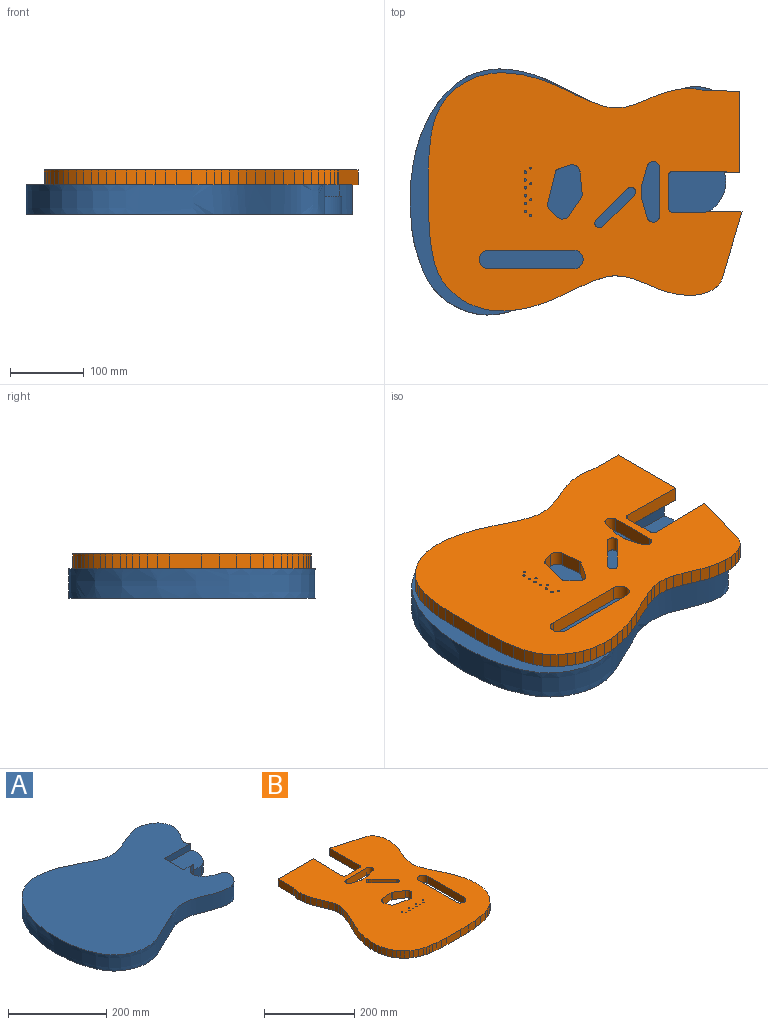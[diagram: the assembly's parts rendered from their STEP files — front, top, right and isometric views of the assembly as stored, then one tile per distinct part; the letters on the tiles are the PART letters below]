
ASSEMBLY  parts=2 mates=1
PART A: 11 faces, bbox 445.4x335.9x40 mm
  f0: plane 50x16mm, normal (1,0,0), area 800mm2, adj f1,f6,f9,f10
  f1: plane 445.41x335.86mm, normal (0,0,1), area 106671.7mm2, adj f0,f2,f4,f5,f7,f9,f10
  f2: extruded ~442.1x331.43mm, area 53327mm2, adj f1,f3,f5,f6,f7,f8
  f3: plane 445.41x335.86mm, normal (0,0,-1), area 110689mm2, adj f2,f7,f8
  f4: plane 25.33x16mm, normal (-0.01,1,0), area 405.4mm2, adj f1,f6,f7,f10
  f5: plane 72.36x16mm, normal (-0.01,-1,0), area 1157.8mm2, adj f1,f2,f6,f9
  f6: plane 78.66x55.93mm, normal (0,0,1), area 4002.8mm2, adj f0,f2,f4,f5,f8,f9,f10
  f7: plane 40x0.32mm, normal (0.99,-0.13,0), area 12.8mm2, adj f1,f2,f3,f4,f8
  f8: plane 24x22.41mm, normal (0.01,-1,0), area 538mm2, adj f2,f3,f6,f7
  f9: cylinder r=3mm len=16mm, axis (0,0,-1), area 74.9mm2, adj f0,f1,f5,f6
  f10: cylinder r=3mm len=16mm, axis (0,0,-1), area 74.9mm2, adj f0,f1,f4,f6
PART B: 125 faces, bbox 324x426.6x20 mm
  f0: plane 20x4.05mm, normal (0.34,0.94,0), area 86.3mm2, adj f98,f117,f118,f122
  f1: cylinder r=6.35mm len=20mm, axis (0,0,-1), area 189.6mm2, adj f114,f117,f118,f124
  f2: cylinder r=6.35mm len=20mm, axis (0,0,-1), area 34.9mm2, adj f3,f116,f117,f118
  f3: plane 25x20mm, normal (0.27,0.96,0), area 519.5mm2, adj f2,f4,f117,f118
  f4: cylinder r=8.71mm len=20mm, axis (0,0,-1), area 499.5mm2, adj f3,f5,f117,f118
  f5: plane 65.13x20mm, normal (0,-1,0), area 1302.5mm2, adj f4,f6,f117,f118
  f6: cylinder r=8.71mm len=20mm, axis (0,0,-1), area 499.5mm2, adj f5,f7,f117,f118
  f7: plane 25x20mm, normal (-0.27,0.96,0), area 519.5mm2, adj f6,f8,f117,f118
  f8: cylinder r=6.35mm len=20mm, axis (0,0,-1), area 34.9mm2, adj f7,f116,f117,f118
  f9: cylinder r=6.73mm len=20mm, axis (0,0,-1), area 134.8mm2, adj f10,f102,f117,f118
  f10: plane 42.31x20mm, normal (0.24,0.97,0), area 872.1mm2, adj f9,f11,f117,f118
  f11: cylinder r=6.73mm len=20mm, axis (0,0,-1), area 134.8mm2, adj f10,f12,f117,f118
  f12: plane 20x15.05mm, normal (0.95,0.32,0), area 317.5mm2, adj f11,f13,f117,f118
  f13: cylinder r=10.92mm len=20mm, axis (0,0,-1), area 393.9mm2, adj f12,f14,f117,f118
  f14: plane 29.83x20mm, normal (0.09,-1,0), area 599mm2, adj f13,f15,f117,f118
  f15: cylinder r=6.73mm len=20mm, axis (0,0,-1), area 90.9mm2, adj f14,f16,f117,f118
  f16: plane 24.94x20mm, normal (-0.55,-0.83,0), area 597.4mm2, adj f15,f17,f117,f118
  f17: cylinder r=10.92mm len=20mm, axis (0,0,-1), area 393.7mm2, adj f16,f102,f117,f118
  f18: cylinder r=12.7mm len=25.4mm, axis (0,0,-1), area 798mm2, adj f19,f103,f117,f118
  f19: plane 116.08x20mm, normal (-1,0,0), area 2321.6mm2, adj f18,f20,f117,f118
  f20: cylinder r=12.7mm len=25.4mm, axis (0,0,-1), area 798mm2, adj f19,f103,f117,f118
  f21: cylinder r=6.35mm len=20mm, axis (0,0,-1), area 194mm2, adj f114,f117,f118,f120
  f22: plane 20x8.11mm, normal (-0.97,0.23,0), area 166.6mm2, adj f23,f117,f118,f119
  f23: plane 20x9.22mm, normal (-0.99,0.1,0), area 185.3mm2, adj f22,f24,f117,f118
  f24: plane 20x10.36mm, normal (-1,-0.01,0), area 207.3mm2, adj f23,f25,f117,f118
  f25: plane 20x11.54mm, normal (-0.99,-0.12,0), area 232.7mm2, adj f24,f26,f117,f118
  f26: plane 20x12.72mm, normal (-0.97,-0.24,0), area 262.2mm2, adj f25,f27,f117,f118
  f27: plane 20x13.71mm, normal (-0.94,-0.34,0), area 291mm2, adj f26,f28,f117,f118
  f28: plane 20x14.18mm, normal (-0.92,-0.38,0), area 307.1mm2, adj f27,f29,f117,f118
  f29: plane 20x13.85mm, normal (-0.93,-0.37,0), area 298.3mm2, adj f28,f30,f117,f118
  f30: plane 20x12.77mm, normal (-0.96,-0.29,0), area 266.5mm2, adj f29,f31,f117,f118
  f31: plane 20x11.39mm, normal (-0.99,-0.13,0), area 229.7mm2, adj f30,f32,f117,f118
  f32: plane 20x10.19mm, normal (-1,0.06,0), area 204.1mm2, adj f31,f33,f117,f118
  f33: plane 20x9.45mm, normal (-0.98,0.21,0), area 193.3mm2, adj f32,f34,f117,f118
  f34: plane 20x18.07mm, normal (-0.94,0.33,0), area 382.4mm2, adj f33,f35,f117,f118
  f35: plane 20x17.87mm, normal (-0.91,0.41,0), area 392.6mm2, adj f34,f36,f117,f118
  f36: plane 20x18.39mm, normal (-0.9,0.44,0), area 409.3mm2, adj f35,f37,f117,f118
  f37: plane 20x19.13mm, normal (-0.92,0.4,0), area 417mm2, adj f36,f38,f117,f118
  f38: plane 20x18.13mm, normal (-0.94,0.33,0), area 384.7mm2, adj f37,f39,f117,f118
  f39: plane 20x16.67mm, normal (-0.97,0.25,0), area 343.9mm2, adj f38,f40,f117,f118
  f40: plane 20x17.8mm, normal (-0.99,0.14,0), area 359.3mm2, adj f39,f41,f117,f118
  f41: plane 20x12.37mm, normal (-1,0.05,0), area 247.7mm2, adj f40,f42,f117,f118
  f42: plane 20x11.55mm, normal (-1,-0.05,0), area 231.2mm2, adj f41,f43,f117,f118
  f43: plane 20x10.2mm, normal (-0.99,-0.16,0), area 206.7mm2, adj f42,f44,f117,f118
  f44: plane 20x13.46mm, normal (-0.96,-0.28,0), area 280.2mm2, adj f43,f45,f117,f118
  f45: plane 20x12.96mm, normal (-0.91,-0.41,0), area 284.4mm2, adj f44,f46,f117,f118
  f46: plane 20x6.84mm, normal (-0.85,-0.52,0), area 160.6mm2, adj f45,f47,f117,f118
  f47: plane 20x7.21mm, normal (-0.8,-0.6,0), area 180.2mm2, adj f46,f48,f117,f118
  f48: plane 20x7.52mm, normal (-0.74,-0.67,0), area 203.8mm2, adj f47,f49,f117,f118
  f49: plane 20x8.84mm, normal (-0.65,-0.76,0), area 233.7mm2, adj f48,f50,f117,f118
  f50: plane 20x7.47mm, normal (-0.56,-0.83,0), area 179.6mm2, adj f49,f51,f117,f118
  f51: plane 20x9.22mm, normal (-0.46,-0.89,0), area 207.3mm2, adj f50,f52,f117,f118
  f52: plane 20x11.57mm, normal (-0.35,-0.94,0), area 246.8mm2, adj f51,f53,f117,f118
  f53: plane 20x6.99mm, normal (-0.27,-0.96,0), area 144.9mm2, adj f52,f54,f117,f118
  f54: plane 20x8.09mm, normal (-0.21,-0.98,0), area 165.4mm2, adj f53,f55,f117,f118
  f55: plane 20x9.49mm, normal (-0.16,-0.99,0), area 192.2mm2, adj f54,f56,f117,f118
  f56: plane 20x11.26mm, normal (-0.11,-0.99,0), area 226.7mm2, adj f55,f57,f117,f118
  f57: plane 20x13.47mm, normal (-0.08,-1,0), area 270.2mm2, adj f56,f58,f117,f118
  f58: plane 20x16.18mm, normal (-0.04,-1,0), area 324mm2, adj f57,f59,f117,f118
  f59: plane 43.54x20mm, normal (0,-1,0), area 870.8mm2, adj f58,f60,f117,f118
  f60: plane 24.61x20mm, normal (0.03,-1,0), area 492.3mm2, adj f59,f61,f117,f118
  f61: plane 22.94x20mm, normal (0.06,-1,0), area 459.7mm2, adj f60,f62,f117,f118
  f62: plane 20.06x20mm, normal (0.13,-0.99,0), area 404.5mm2, adj f61,f63,f117,f118
  f63: plane 20x16.76mm, normal (0.22,-0.98,0), area 343.6mm2, adj f62,f64,f117,f118
  f64: plane 20x13.56mm, normal (0.34,-0.94,0), area 288.5mm2, adj f63,f65,f117,f118
  f65: plane 20x10.83mm, normal (0.48,-0.88,0), area 246.9mm2, adj f64,f66,f117,f118
  f66: plane 20x8.81mm, normal (0.61,-0.79,0), area 222.5mm2, adj f65,f67,f117,f118
  f67: plane 20x7.42mm, normal (0.71,-0.7,0), area 209.1mm2, adj f66,f68,f117,f118
  f68: plane 20x10.27mm, normal (0.79,-0.61,0), area 260.2mm2, adj f67,f69,f117,f118
  f69: plane 20x10.03mm, normal (0.86,-0.51,0), area 232.9mm2, adj f68,f70,f117,f118
  f70: plane 20x9.7mm, normal (0.92,-0.4,0), area 211.6mm2, adj f69,f71,f117,f118
  f71: plane 20x9.98mm, normal (0.95,-0.3,0), area 209.3mm2, adj f70,f72,f117,f118
  f72: plane 20x11.06mm, normal (0.98,-0.2,0), area 225.7mm2, adj f71,f73,f117,f118
  f73: plane 20x12.75mm, normal (1,-0.08,0), area 255.8mm2, adj f72,f74,f117,f118
  f74: plane 20x14.01mm, normal (1,0.04,0), area 280.4mm2, adj f73,f75,f117,f118
  f75: plane 20x13.73mm, normal (0.99,0.12,0), area 276.5mm2, adj f74,f76,f117,f118
  f76: plane 20x12.74mm, normal (0.98,0.2,0), area 260.1mm2, adj f75,f77,f117,f118
  f77: plane 20x12.84mm, normal (0.96,0.28,0), area 267.6mm2, adj f76,f78,f117,f118
  f78: plane 20x13.94mm, normal (0.94,0.34,0), area 296.7mm2, adj f77,f79,f117,f118
  f79: plane 20x14.55mm, normal (0.92,0.39,0), area 316mm2, adj f78,f80,f117,f118
  f80: plane 21.12x20mm, normal (0.9,0.43,0), area 468.9mm2, adj f79,f81,f117,f118
  f81: plane 20.35x20mm, normal (0.91,0.41,0), area 447.4mm2, adj f80,f82,f117,f118
  f82: plane 20x10.22mm, normal (0.94,0.35,0), area 218mm2, adj f81,f83,f117,f118
  f83: plane 20x10.44mm, normal (0.96,0.28,0), area 217.3mm2, adj f82,f84,f117,f118
  f84: plane 20x11.04mm, normal (0.99,0.15,0), area 223.5mm2, adj f83,f85,f117,f118
  f85: plane 20x12.29mm, normal (1,-0.04,0), area 246mm2, adj f84,f86,f117,f118
  f86: plane 20x11.09mm, normal (0.97,-0.23,0), area 227.8mm2, adj f85,f87,f117,f118
  f87: plane 20x12.16mm, normal (0.94,-0.34,0), area 258.4mm2, adj f86,f88,f117,f118
  f88: plane 20x12.83mm, normal (0.92,-0.38,0), area 278mm2, adj f87,f89,f117,f118
  f89: plane 20x12.85mm, normal (0.93,-0.38,0), area 277.2mm2, adj f88,f90,f117,f118
  f90: plane 20x12.32mm, normal (0.95,-0.32,0), area 260mm2, adj f89,f91,f117,f118
  f91: plane 20x14.15mm, normal (0.98,-0.22,0), area 289.9mm2, adj f90,f92,f117,f118
  f92: plane 20x12.57mm, normal (1,-0.09,0), area 252.5mm2, adj f91,f93,f117,f118
  f93: plane 20x11.04mm, normal (1,0.03,0), area 220.8mm2, adj f92,f94,f117,f118
  f94: plane 20x9.63mm, normal (0.99,0.16,0), area 195.2mm2, adj f93,f95,f117,f118
  f95: plane 20x8.39mm, normal (0.95,0.32,0), area 177.4mm2, adj f94,f96,f117,f118
  f96: plane 20x7.16mm, normal (0.87,0.5,0), area 165.3mm2, adj f95,f97,f117,f118
  f97: plane 20x5.67mm, normal (0.75,0.66,0), area 151mm2, adj f96,f98,f117,f118
  f98: plane 20x5.18mm, normal (0.59,0.81,0), area 128.4mm2, adj f0,f97,f117,f118
  f99: cylinder r=6.35mm len=20mm, axis (0,0,-1), area 399mm2, adj f100,f115,f117,f118
  f100: plane 42.66x42.66mm, normal (0.71,0.71,0), area 1206.5mm2, adj f99,f101,f117,f118
  f101: cylinder r=6.35mm len=20mm, axis (0,0,-1), area 399mm2, adj f100,f115,f117,f118
  f102: plane 20x11.55mm, normal (-0.69,0.73,0), area 317.5mm2, adj f9,f17,f117,f118
  f103: plane 116.08x20mm, normal (1,0,0), area 2321.6mm2, adj f18,f20,f117,f118
  f104: cylinder r=1.38mm len=20mm, axis (0,0,-1), area 174mm2, adj f117,f118
  f105: cylinder r=1.38mm len=20mm, axis (0,0,-1), area 174mm2, adj f117,f118
  f106: cylinder r=1.59mm len=20mm, axis (0,0,-1), area 199.5mm2, adj f117,f118
  f107: cylinder r=1.59mm len=20mm, axis (0,0,-1), area 199.5mm2, adj f117,f118
  f108: cylinder r=1.59mm len=20mm, axis (0,0,-1), area 199.5mm2, adj f117,f118
  f109: cylinder r=1.59mm len=20mm, axis (0,0,-1), area 199.5mm2, adj f117,f118
  f110: cylinder r=1.59mm len=20mm, axis (0,0,-1), area 199.5mm2, adj f117,f118
  f111: cylinder r=1.59mm len=20mm, axis (0,0,-1), area 199.5mm2, adj f117,f118
  f112: cylinder r=1.38mm len=20mm, axis (0,0,-1), area 174mm2, adj f117,f118
  f113: cylinder r=1.38mm len=20mm, axis (0,0,-1), area 174mm2, adj f117,f118
  f114: plane 43.18x20mm, normal (0,1,0), area 863.6mm2, adj f1,f21,f117,f118
  f115: plane 42.66x42.66mm, normal (-0.71,-0.71,0), area 1206.5mm2, adj f99,f101,f117,f118
  f116: plane 20x16.41mm, normal (0,1,0), area 328.1mm2, adj f2,f8,f117,f118
  f117: plane 426.61x324mm, normal (0,0,1), area 100537.9mm2, adj f0,f1,f2,f3,f4,f5,f6,f7
  f118: plane 426.61x324mm, normal (0,0,-1), area 100537.9mm2, adj f0,f1,f2,f3,f4,f5,f6,f7
  f119: plane 48.37x20mm, normal (-1,0.01,0), area 967.5mm2, adj f22,f117,f118,f121
  f120: plane 91.49x20mm, normal (1,-0.01,0), area 1830mm2, adj f21,f117,f118,f121
  f121: plane 110.19x20mm, normal (0,1,0), area 2203.7mm2, adj f117,f118,f119,f120
  f122: plane 20x0.1mm, normal (0.94,-0.33,0), area 2.2mm2, adj f0,f117,f118,f123
  f123: plane 90.86x26.87mm, normal (0.28,0.96,0), area 1895.1mm2, adj f117,f118,f122,f124
  f124: plane 94.44x20mm, normal (-1,-0.01,0), area 1889mm2, adj f1,f117,f118,f123
PLACE A t=(4.19,0.22,0)mm
PLACE B rot(axis=(0,0,-1),90deg) t=(11.4,0.22,40)mm
MATE fastened B.f118 <-> A.f1  axis (0,0,-1) through (134.88,0.22,40)mm
